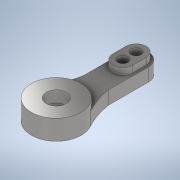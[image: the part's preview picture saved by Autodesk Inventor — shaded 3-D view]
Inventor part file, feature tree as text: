
AUTODESK INVENTOR PART (.ipt)
format: ipt  version: 2020 (Build 240168000, 168)  size: 163,840 bytes
history: native  units: in
note: dims shown in document units (in); Inventor stores cm internally (conversion verified against a paired STEP export)
features: extrude x4, sketch x4, projected_geometry x1
ambient origin geometry x8: Origin, YZ Plane, XZ Plane, XY Plane, X Axis, Y Axis, Z Axis, Center Point
bodies: Solid1 (feature_tree)
feature tree (9):
  extrude  "Extrusion1"  Depth=0.9449in
  extrude  "Extrusion2"  Depth=1.0236in
  extrude  "Extrusion3"  Depth=0.1181in
  extrude  "Extrusion4"  Depth=0.2362in TaperAngle=0.0deg
  sketch  "Sketch1"  dims[d0=0.5906in d1=0.9449in]
  sketch  "Sketch2"  dims[d2=0.2953in d3=1.0236in]
  projected_geometry  "Projected Loop1"
  sketch  "Sketch3"  dims[d4=0.1181in d5=0.1181in]
  sketch  "Sketch4"  dims[d6=0.7874in d7=0.2362in d8=0.0in d9=0.2362in d10=0.0787in d11=0.0in d12=0.2362in d13=0.0in d14=0.0in d15=0.1181in d16=0.0984in d17=0.0in]
